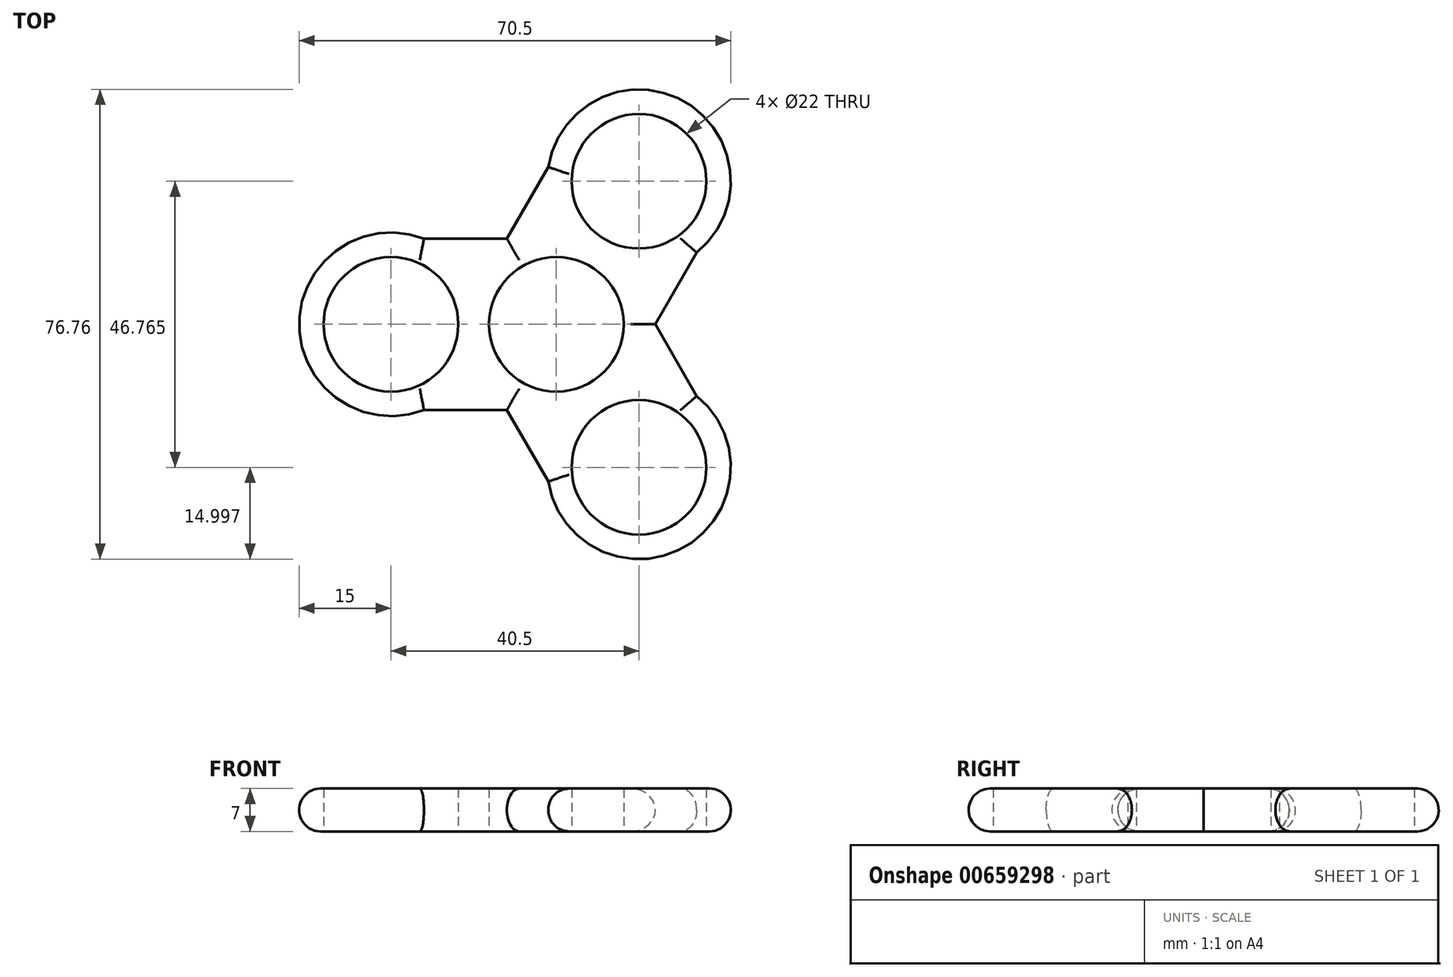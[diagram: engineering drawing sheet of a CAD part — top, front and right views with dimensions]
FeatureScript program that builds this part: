
annotation { "Feature Type Name" : "Feature", "Feature Type Description" : "" }
export const myFeature = defineFeature(function(context is Context, id is Id, definition is map)
    precondition{}
    {
        {
            var Q0;
            Q0=qCreatedBy(makeId("Front.planeOp"),FACE);
            var sketch = newSketch(context, id + "F0", { "sketchPlane" : qUnion([Q0])});
            skLineSegment(sketch, "E0", {"start": v(0, 0) * mm, "end": v(0, 6.18) * mm});
            skSolve(sketch);
        }
        {
            var Q0;
            Q0=qCreatedBy(makeId("Top.planeOp"),FACE);
            var sketch = newSketch(context, id + "F1", { "sketchPlane" : qUnion([Q0])});
            skArc(sketch, "E1", {"start": v(0, 11) * mm, "mid": v(-11, 0) * mm, "end": v(0, -11) * mm});
            skLineSegment(sketch, "E2", {"start": v(0, 56.07) * mm, "end": v(0, 11) * mm, "construction": true});
            skLineSegment(sketch, "E3", {"start": v(-42, 56.32) * mm, "end": v(-42, -55.95) * mm, "construction": true});
            skArc(sketch, "E4", {"start": v(-21.61, 14) * mm, "mid": v(-42, 0) * mm, "end": v(-21.61, -14) * mm});
            skLineSegment(sketch, "E5", {"start": v(0, 14) * mm, "end": v(-21.61, 14) * mm});
            skLineSegment(sketch, "E6", {"start": v(0, -14) * mm, "end": v(-21.61, -14) * mm});
            skLineSegment(sketch, "E7", {"start": v(0, 14) * mm, "end": v(0, 11) * mm});
            skLineSegment(sketch, "E8.trimOffspring", {"start": v(0, -11) * mm, "end": v(0, -55.82) * mm, "construction": true});
            skLineSegment(sketch, "E9.trimOffspring", {"start": v(0, -11) * mm, "end": v(0, -14) * mm});
            skCircle(sketch, "E10", {"center": v(-27, 0) * mm, "radius": 11 * mm});
            skSolve(sketch);
        }
        {
            var Q0;
            Q0=qSketchRegion(id+"F1",true);
            extrude(context, id + "F2", {"entities" : qUnion([Q0]), "depth" : 7 * mm, "offsetDistance" : 25 * mm});
        }
        {
            var Q0;
            Q0=makeQuery(id+"F2.opExtrude","SWEPT_BODY",BODY,{"disambiguationData":[OSD([sQuery(id+"F1.wireOp",EDGE,"E1"),sQuery(id+"F1.wireOp",EDGE,"E4"),sQuery(id+"F1.wireOp",EDGE,"E5"),sQuery(id+"F1.wireOp",EDGE,"E6"),sQuery(id+"F1.wireOp",EDGE,"E7"),sQuery(id+"F1.wireOp",EDGE,"E9.trimOffspring"),sQuery(id+"F1.wireOp",EDGE,"E10")])]});
            var Q1;
            Q1=sQuery(id+"F0.wireOp",EDGE,"E0");
            circularPattern(context, id + "F3", {"operationType" : NewBodyOperationType.ADD, "entities" : qUnion([Q0]), "axis" : qUnion([Q1]), "angle" : 240 * degree, "instanceCount" : 3, "equalSpace" : true});
        }
        {
            var Q0;
            Q0=makeQuery(id+"F2.opExtrude","CAP_EDGE",EDGE,{"disambiguationData":[OSD([sQuery(id+"F1.wireOp",EDGE,"E4")])],"isStart":false});
            var Q1;
            Q1=makeQuery(id+"F2.opExtrude","CAP_EDGE",EDGE,{"disambiguationData":[OSD([sQuery(id+"F1.wireOp",EDGE,"E6")])],"isStart":false});
            var Q2;
            Q2=makeQuery(id+"F3.opPattern","COPY",EDGE,{"derivedFrom":makeQuery(id+"F2.opExtrude","CAP_EDGE",EDGE,{"disambiguationData":[OSD([sQuery(id+"F1.wireOp",EDGE,"E5")])],"isStart":false}),"instanceName":"1"});
            var Q3;
            Q3=makeQuery(id+"F3.opPattern","COPY",EDGE,{"derivedFrom":makeQuery(id+"F2.opExtrude","CAP_EDGE",EDGE,{"disambiguationData":[OSD([sQuery(id+"F1.wireOp",EDGE,"E4")])],"isStart":false}),"instanceName":"1"});
            var Q4;
            Q4=makeQuery(id+"F3.opPattern","COPY",EDGE,{"derivedFrom":makeQuery(id+"F2.opExtrude","CAP_EDGE",EDGE,{"disambiguationData":[OSD([sQuery(id+"F1.wireOp",EDGE,"E6")])],"isStart":false}),"instanceName":"1"});
            var Q5;
            Q5=makeQuery(id+"F3.opPattern","COPY",EDGE,{"derivedFrom":makeQuery(id+"F2.opExtrude","CAP_EDGE",EDGE,{"disambiguationData":[OSD([sQuery(id+"F1.wireOp",EDGE,"E5")])],"isStart":false}),"instanceName":"2"});
            var Q6;
            Q6=makeQuery(id+"F3.opPattern","COPY",EDGE,{"derivedFrom":makeQuery(id+"F2.opExtrude","CAP_EDGE",EDGE,{"disambiguationData":[OSD([sQuery(id+"F1.wireOp",EDGE,"E6")])],"isStart":false}),"instanceName":"2"});
            var Q7;
            Q7=makeQuery(id+"F2.opExtrude","CAP_EDGE",EDGE,{"disambiguationData":[OSD([sQuery(id+"F1.wireOp",EDGE,"E5")])],"isStart":false});
            var Q8;
            Q8=makeQuery(id+"F3.opPattern","COPY",EDGE,{"derivedFrom":makeQuery(id+"F2.opExtrude","CAP_EDGE",EDGE,{"disambiguationData":[OSD([sQuery(id+"F1.wireOp",EDGE,"E4")])],"isStart":false}),"instanceName":"2"});
            var Q9;
            Q9=makeQuery(id+"F2.opExtrude","CAP_EDGE",EDGE,{"disambiguationData":[OSD([sQuery(id+"F1.wireOp",EDGE,"E6")])],"isStart":true});
            var Q10;
            Q10=makeQuery(id+"F3.opPattern","COPY",EDGE,{"derivedFrom":makeQuery(id+"F2.opExtrude","CAP_EDGE",EDGE,{"disambiguationData":[OSD([sQuery(id+"F1.wireOp",EDGE,"E5")])],"isStart":true}),"instanceName":"1"});
            var Q11;
            Q11=makeQuery(id+"F2.opExtrude","CAP_EDGE",EDGE,{"disambiguationData":[OSD([sQuery(id+"F1.wireOp",EDGE,"E4")])],"isStart":true});
            var Q12;
            Q12=makeQuery(id+"F2.opExtrude","CAP_EDGE",EDGE,{"disambiguationData":[OSD([sQuery(id+"F1.wireOp",EDGE,"E5")])],"isStart":true});
            var Q13;
            Q13=makeQuery(id+"F3.opPattern","COPY",EDGE,{"derivedFrom":makeQuery(id+"F2.opExtrude","CAP_EDGE",EDGE,{"disambiguationData":[OSD([sQuery(id+"F1.wireOp",EDGE,"E6")])],"isStart":true}),"instanceName":"2"});
            var Q14;
            Q14=makeQuery(id+"F3.opPattern","COPY",EDGE,{"derivedFrom":makeQuery(id+"F2.opExtrude","CAP_EDGE",EDGE,{"disambiguationData":[OSD([sQuery(id+"F1.wireOp",EDGE,"E4")])],"isStart":true}),"instanceName":"2"});
            var Q15;
            Q15=makeQuery(id+"F3.opPattern","COPY",EDGE,{"derivedFrom":makeQuery(id+"F2.opExtrude","CAP_EDGE",EDGE,{"disambiguationData":[OSD([sQuery(id+"F1.wireOp",EDGE,"E5")])],"isStart":true}),"instanceName":"2"});
            var Q16;
            Q16=makeQuery(id+"F3.opPattern","COPY",EDGE,{"derivedFrom":makeQuery(id+"F2.opExtrude","CAP_EDGE",EDGE,{"disambiguationData":[OSD([sQuery(id+"F1.wireOp",EDGE,"E6")])],"isStart":true}),"instanceName":"1"});
            var Q17;
            Q17=makeQuery(id+"F3.opPattern","COPY",EDGE,{"derivedFrom":makeQuery(id+"F2.opExtrude","CAP_EDGE",EDGE,{"disambiguationData":[OSD([sQuery(id+"F1.wireOp",EDGE,"E4")])],"isStart":true}),"instanceName":"1"});
            fillet(context, id + "F4", {"entities" : qUnion([Q0, Q1, Q2, Q3, Q4, Q5, Q6, Q7, Q8, Q9, Q10, Q11, Q12, Q13, Q14, Q15, Q16, Q17]), "radius" : 3.5 * mm, "tangentPropagation" : true, "allowEdgeOverflow" : false});
        }
    });
